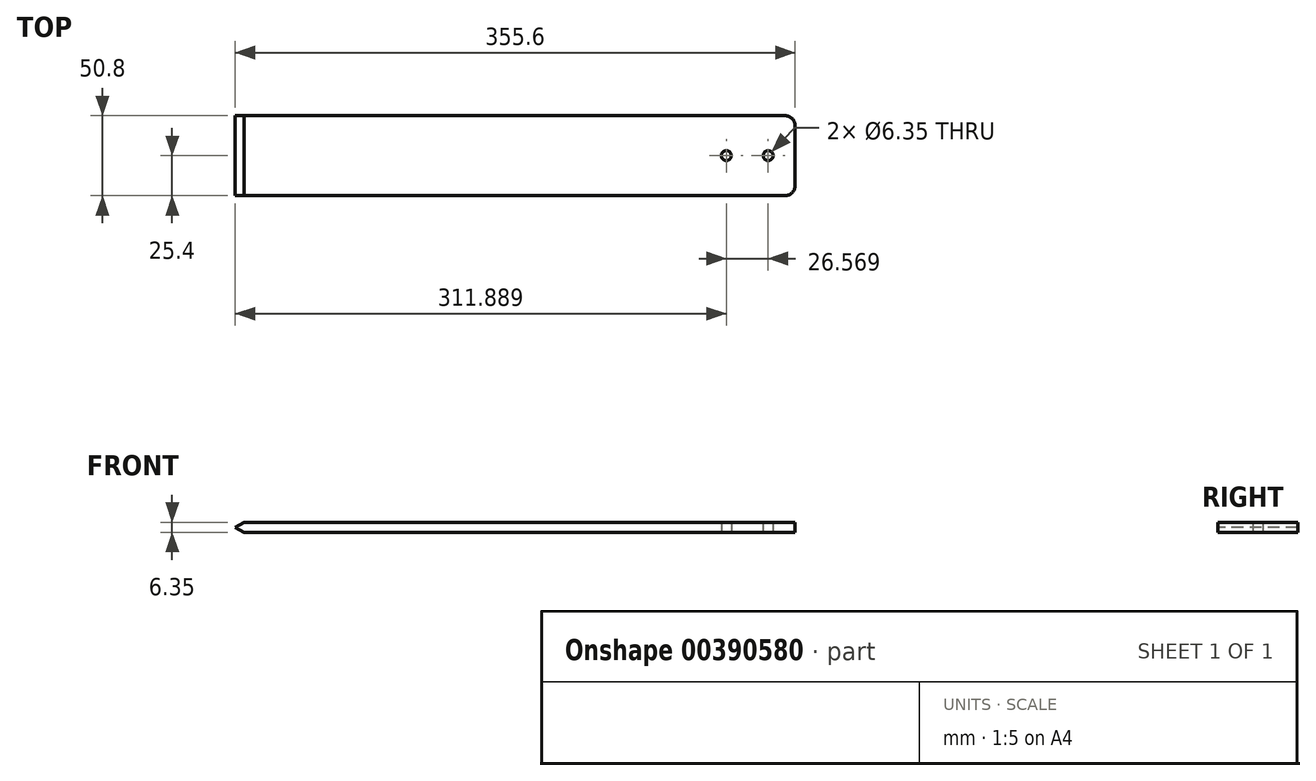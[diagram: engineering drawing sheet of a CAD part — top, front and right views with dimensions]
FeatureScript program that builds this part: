
annotation { "Feature Type Name" : "Feature", "Feature Type Description" : "" }
export const myFeature = defineFeature(function(context is Context, id is Id, definition is map)
    precondition{}
    {
        {
            var Q0;
            Q0=qCreatedBy(makeId("Top.planeOp"),FACE);
            var sketch = newSketch(context, id + "F0", { "sketchPlane" : qUnion([Q0])});
            skLineSegment(sketch, "E0.bottom", {"start": v(177.8, -25.4) * mm, "end": v(-177.8, -25.4) * mm});
            skLineSegment(sketch, "E0.top", {"start": v(177.8, 25.4) * mm, "end": v(-177.8, 25.4) * mm});
            skLineSegment(sketch, "E0.left", {"start": v(177.8, -25.4) * mm, "end": v(177.8, 25.4) * mm});
            skLineSegment(sketch, "E0.right", {"start": v(-177.8, -25.4) * mm, "end": v(-177.8, 25.4) * mm});
            skPoint(sketch, "E0.middle", {"position": v(0, 0) * mm});
            skCircle(sketch, "E1", {"center": v(160.66, 0) * mm, "radius": 3.18 * mm});
            skCircle(sketch, "E2", {"center": v(134.09, 0) * mm, "radius": 3.18 * mm});
            skSolve(sketch);
        }
        {
            var Q0;
            Q0 = qSketchRegion(id + "F0", true);
            extrude(context, id + "F1", {"entities" : qUnion([Q0]), "depth" : 6.35 * mm});
        }
        {
            var Q0;
            Q0=makeQuery(id+"F1.opExtrude","SWEPT_EDGE",EDGE,{"disambiguationData":[OSD([sQuery(id+"F0.wireOp",EDGE,"E0.bottom"),sQuery(id+"F0.wireOp",EDGE,"E0.left")])]});
            var Q1;
            Q1=makeQuery(id+"F1.opExtrude","SWEPT_EDGE",EDGE,{"disambiguationData":[OSD([sQuery(id+"F0.wireOp",EDGE,"E0.top"),sQuery(id+"F0.wireOp",EDGE,"E0.left")])]});
            fillet(context, id + "F2", {"entities" : qUnion([Q0, Q1]), "radius" : 6.35 * mm, "tangentPropagation" : true, "allowEdgeOverflow" : false});
        }
        {
            var Q0;
            Q0=makeQuery(id+"F1.opExtrude","SWEPT_FACE",FACE,{"disambiguationData":[OSD([sQuery(id+"F0.wireOp",EDGE,"E0.bottom")])]});
            var sketch = newSketch(context, id + "F3", { "sketchPlane" : qUnion([Q0])});
            skLineSegment(sketch, "E3", {"start": v(-177.8, 3.17) * mm, "end": v(-172.3, 6.35) * mm});
            skLineSegment(sketch, "E4", {"start": v(-177.8, 3.18) * mm, "end": v(-177.8, 6.35) * mm});
            skLineSegment(sketch, "E5", {"start": v(-177.8, 6.35) * mm, "end": v(-172.3, 6.35) * mm});
            skLineSegment(sketch, "E6", {"start": v(-177.8, 3.18) * mm, "end": v(-172.3, 0) * mm});
            skLineSegment(sketch, "E7", {"start": v(-172.3, 0) * mm, "end": v(-177.8, 0) * mm});
            skLineSegment(sketch, "E8", {"start": v(-177.8, 0) * mm, "end": v(-177.8, 3.18) * mm});
            skSolve(sketch);
        }
        {
            var Q0;
            Q0 = qSketchRegion(id + "F3", true);
            extrude(context, id + "F4", {"entities" : qUnion([Q0]), "operationType" : NewBodyOperationType.REMOVE, "endBound" : BoundingType.THROUGH_ALL, "oppositeDirection" : true, "depth" : 25.4 * mm});
        }
    });
